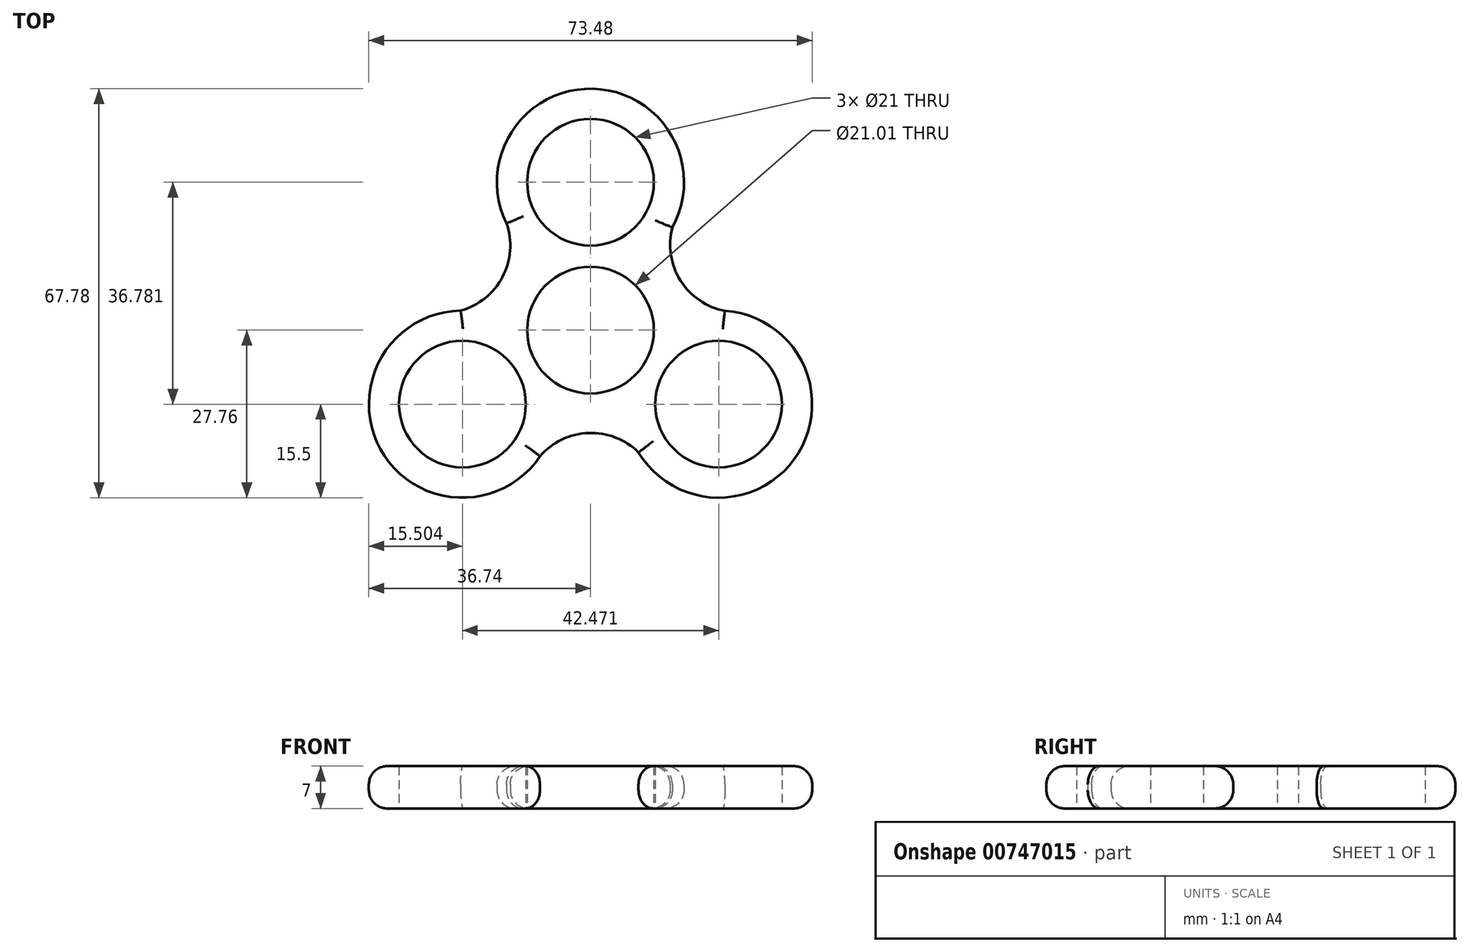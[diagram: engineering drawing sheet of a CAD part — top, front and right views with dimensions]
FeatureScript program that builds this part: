
annotation { "Feature Type Name" : "Feature", "Feature Type Description" : "" }
export const myFeature = defineFeature(function(context is Context, id is Id, definition is map)
    precondition{}
    {
        {
            var Q0;
            Q0=qCreatedBy(makeId("Top.planeOp"),FACE);
            var sketch = newSketch(context, id + "F0", { "sketchPlane" : qUnion([Q0])});
            skCircle(sketch, "E0", {"center": v(0, 47.38) * mm, "radius": 10.5 * mm});
            skCircle(sketch, "E1.1.0", {"center": v(-21.24, 10.6) * mm, "radius": 10.5 * mm});
            skCircle(sketch, "E1.2.0", {"center": v(21.24, 10.6) * mm, "radius": 10.5 * mm});
            skPoint(sketch, "E1.center", {"position": v(0, 22.86) * mm});
            skCircle(sketch, "E2", {"center": v(0, 22.86) * mm, "radius": 10.5 * mm});
            skArc(sketch, "E3", {"start": v(-21.53, 26.1) * mm, "mid": v(-34.85, 3.18) * mm, "end": v(-8.36, 1.96) * mm});
            skArc(sketch, "E4", {"start": v(7.96, 2.6) * mm, "mid": v(34.47, 2.52) * mm, "end": v(22.28, 26.07) * mm});
            skArc(sketch, "E5.trimOffspring", {"start": v(13.57, 39.88) * mm, "mid": v(0.38, 62.88) * mm, "end": v(-13.92, 40.55) * mm});
            skArc(sketch, "E6", {"start": v(-21.53, 26.1) * mm, "mid": v(-14.58, 31.67) * mm, "end": v(-13.92, 40.55) * mm});
            skArc(sketch, "E7.1.0", {"start": v(7.96, 2.6) * mm, "mid": v(-0.34, 5.82) * mm, "end": v(-8.36, 1.96) * mm});
            skArc(sketch, "E7.2.0", {"start": v(13.57, 39.88) * mm, "mid": v(14.92, 31.08) * mm, "end": v(22.28, 26.07) * mm});
            skSolve(sketch);
        }
        {
            var Q0;
            Q0=makeQuery(id+"F0.imprint","IMPRINT",FACE,{"disambiguationData":[TD([[makeQuery(id+"F0.imprint","IMPRINT",EDGE,{"derivedFrom":sQuery(id+"F0.wireOp",EDGE,"E0")}),-1.0]])]});
            extrude(context, id + "F1", {"entities" : qUnion([Q0]), "depth" : 7 * mm, "offsetDistance" : 25.4 * mm});
        }
        {
            var Q0;
            Q0=makeQuery(id+"F1.opExtrude","CAP_EDGE",EDGE,{"disambiguationData":[OSD([sQuery(id+"F0.wireOp",EDGE,"E7.1.0")])],"isStart":false});
            var Q1;
            Q1=makeQuery(id+"F1.opExtrude","CAP_EDGE",EDGE,{"disambiguationData":[OSD([sQuery(id+"F0.wireOp",EDGE,"E4")])],"isStart":false});
            var Q2;
            Q2=makeQuery(id+"F1.opExtrude","CAP_EDGE",EDGE,{"disambiguationData":[OSD([sQuery(id+"F0.wireOp",EDGE,"E3")])],"isStart":false});
            var Q3;
            Q3=makeQuery(id+"F1.opExtrude","CAP_EDGE",EDGE,{"disambiguationData":[OSD([sQuery(id+"F0.wireOp",EDGE,"E7.2.0")])],"isStart":false});
            var Q4;
            Q4=makeQuery(id+"F1.opExtrude","CAP_EDGE",EDGE,{"disambiguationData":[OSD([sQuery(id+"F0.wireOp",EDGE,"E5.trimOffspring")])],"isStart":false});
            var Q5;
            Q5=makeQuery(id+"F1.opExtrude","CAP_EDGE",EDGE,{"disambiguationData":[OSD([sQuery(id+"F0.wireOp",EDGE,"E6")])],"isStart":false});
            var Q6;
            Q6=makeQuery(id+"F1.opExtrude","CAP_EDGE",EDGE,{"disambiguationData":[OSD([sQuery(id+"F0.wireOp",EDGE,"E4")])],"isStart":true});
            var Q7;
            Q7=makeQuery(id+"F1.opExtrude","CAP_EDGE",EDGE,{"disambiguationData":[OSD([sQuery(id+"F0.wireOp",EDGE,"E7.1.0")])],"isStart":true});
            var Q8;
            Q8=makeQuery(id+"F1.opExtrude","CAP_EDGE",EDGE,{"disambiguationData":[OSD([sQuery(id+"F0.wireOp",EDGE,"E3")])],"isStart":true});
            var Q9;
            Q9=makeQuery(id+"F1.opExtrude","CAP_EDGE",EDGE,{"disambiguationData":[OSD([sQuery(id+"F0.wireOp",EDGE,"E6")])],"isStart":true});
            var Q10;
            Q10=makeQuery(id+"F1.opExtrude","CAP_EDGE",EDGE,{"disambiguationData":[OSD([sQuery(id+"F0.wireOp",EDGE,"E5.trimOffspring")])],"isStart":true});
            var Q11;
            Q11=makeQuery(id+"F1.opExtrude","CAP_EDGE",EDGE,{"disambiguationData":[OSD([sQuery(id+"F0.wireOp",EDGE,"E7.2.0")])],"isStart":true});
            fillet(context, id + "F2", {"entities" : qUnion([Q0, Q1, Q2, Q3, Q4, Q5, Q6, Q7, Q8, Q9, Q10, Q11]), "radius" : 3.05 * mm, "tangentPropagation" : true, "allowEdgeOverflow" : false});
        }
    });
